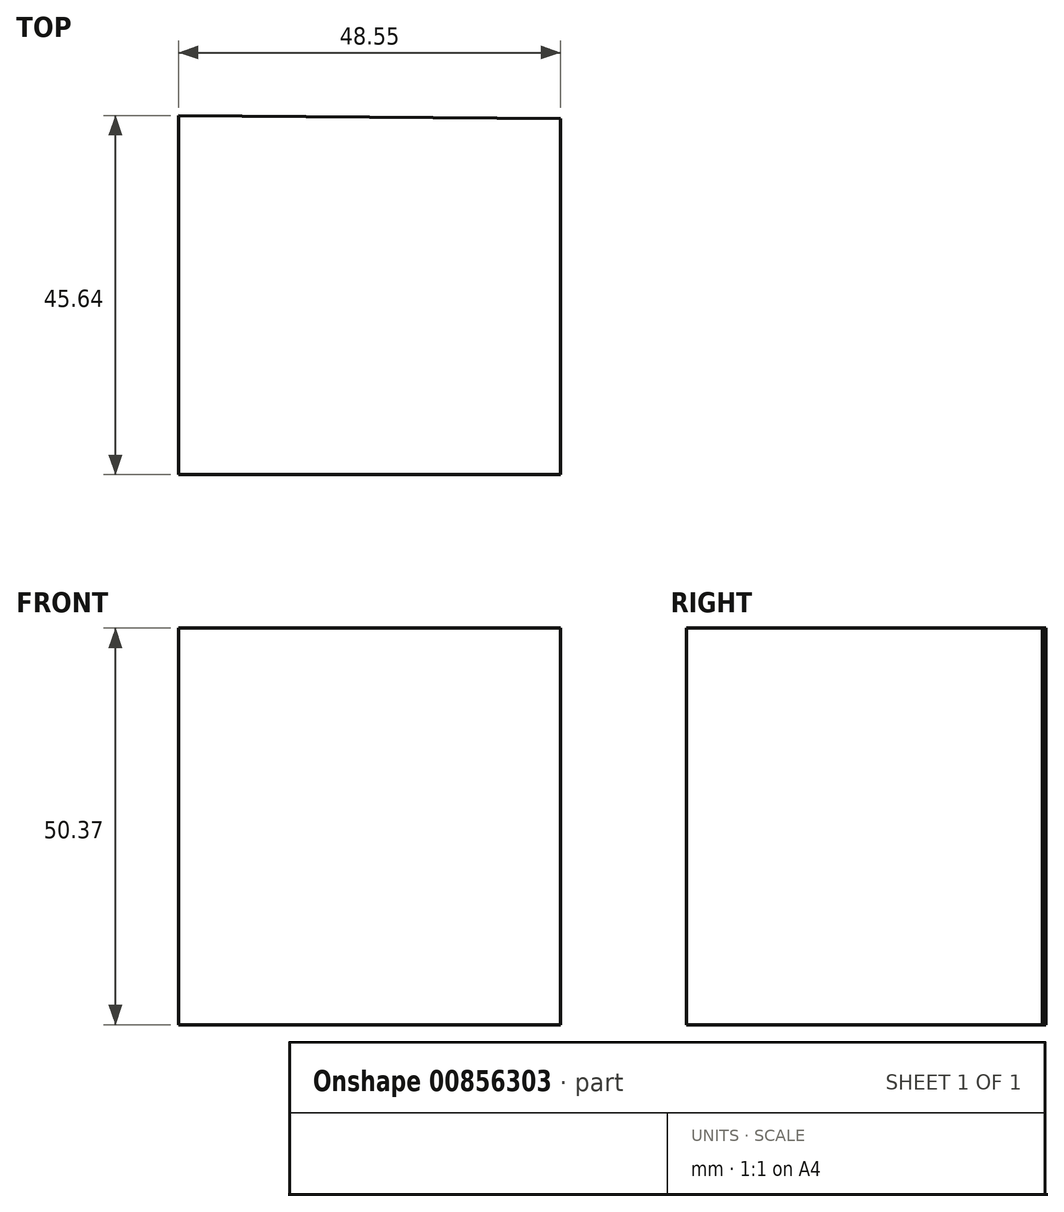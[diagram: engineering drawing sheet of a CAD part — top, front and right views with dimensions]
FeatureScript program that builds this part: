
annotation { "Feature Type Name" : "Feature", "Feature Type Description" : "" }
export const myFeature = defineFeature(function(context is Context, id is Id, definition is map)
    precondition{}
    {
        {
            var Q0;
            Q0=qCreatedBy(makeId("Top.planeOp"),FACE);
            var sketch = newSketch(context, id + "F0", { "sketchPlane" : qUnion([Q0])});
            skLineSegment(sketch, "E0", {"start": v(-25.3, 23.03) * mm, "end": v(-25.3, -22.61) * mm});
            skLineSegment(sketch, "E1", {"start": v(-25.3, -22.61) * mm, "end": v(23.24, -22.61) * mm});
            skLineSegment(sketch, "E2", {"start": v(23.24, -22.61) * mm, "end": v(23.24, 22.61) * mm});
            skLineSegment(sketch, "E3", {"start": v(23.24, 22.61) * mm, "end": v(-25.3, 23.03) * mm});
            skSolve(sketch);
        }
        {
            var Q0;
            Q0=makeQuery(id+"F0.imprint","IMPRINT",FACE,{"disambiguationData":[TD([[makeQuery(id+"F0.imprint","IMPRINT",EDGE,{"derivedFrom":sQuery(id+"F0.wireOp",EDGE,"E0")}),1.0]])]});
            extrude(context, id + "F1", {"entities" : qUnion([Q0]), "oppositeDirection" : true, "depth" : 50.37 * mm, "offsetDistance" : 25.4 * mm});
        }
    });
